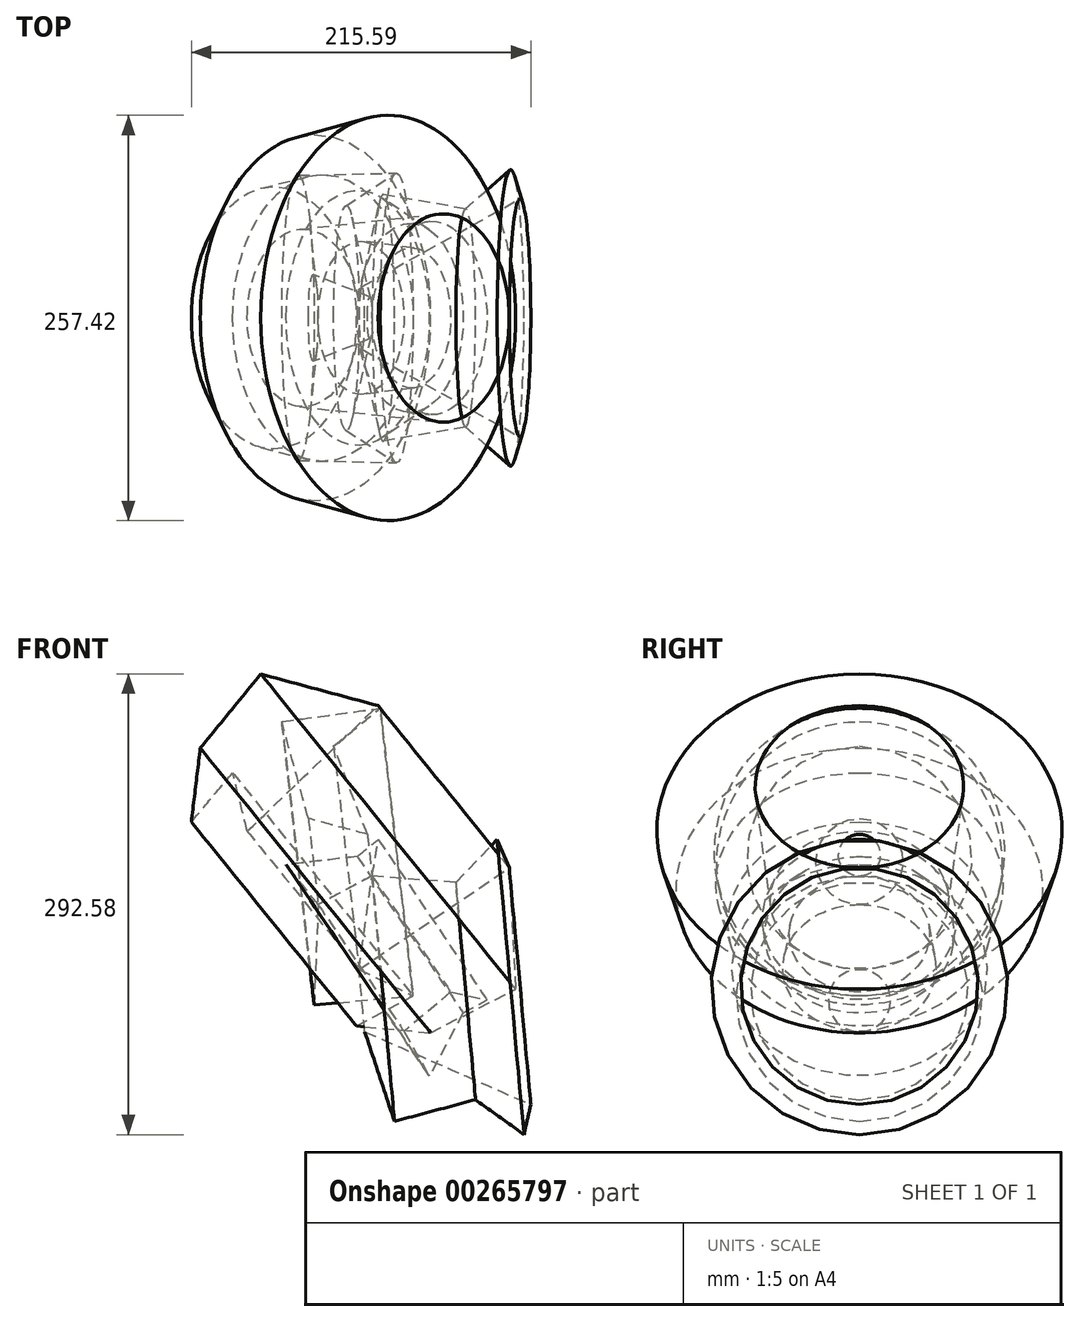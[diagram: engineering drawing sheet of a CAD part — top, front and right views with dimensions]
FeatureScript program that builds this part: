
annotation { "Feature Type Name" : "Feature", "Feature Type Description" : "" }
export const myFeature = defineFeature(function(context is Context, id is Id, definition is map)
    precondition{}
    {
        {
            var Q0;
            Q0=qCreatedBy(makeId("Front.planeOp"),FACE);
            var sketch = newSketch(context, id + "F0", { "sketchPlane" : qUnion([Q0])});
            skLineSegment(sketch, "E0", {"start": v(-31.41, 41.98) * mm, "end": v(-39.7, -17.42) * mm});
            skLineSegment(sketch, "E1", {"start": v(-39.7, -17.42) * mm, "end": v(55.69, 47.12) * mm});
            skLineSegment(sketch, "E2", {"start": v(55.69, 47.12) * mm, "end": v(59.68, -29.99) * mm});
            skLineSegment(sketch, "E3", {"start": v(59.68, -29.99) * mm, "end": v(5.71, -57.69) * mm});
            skLineSegment(sketch, "E4", {"start": v(5.71, -57.69) * mm, "end": v(-41.4, -53.4) * mm});
            skLineSegment(sketch, "E5", {"start": v(-41.4, -53.4) * mm, "end": v(-5.43, -34.27) * mm});
            skLineSegment(sketch, "E6", {"start": v(-5.43, -34.27) * mm, "end": v(-68.25, -39.98) * mm});
            skLineSegment(sketch, "E7", {"start": v(-68.25, -39.98) * mm, "end": v(-65.68, 23.7) * mm});
            skLineSegment(sketch, "E8", {"start": v(-65.68, 23.7) * mm, "end": v(-85.96, 49.12) * mm});
            skLineSegment(sketch, "E9", {"start": v(-85.96, 49.12) * mm, "end": v(-40.84, 54.26) * mm});
            skLineSegment(sketch, "E10", {"start": v(-40.84, 54.26) * mm, "end": v(-27.41, 65.11) * mm});
            skLineSegment(sketch, "E11", {"start": v(-27.41, 65.11) * mm, "end": v(47.98, 65.11) * mm});
            skLineSegment(sketch, "E12", {"start": v(47.98, 65.11) * mm, "end": v(21.7, 37.7) * mm});
            skLineSegment(sketch, "E13", {"start": v(21.7, 37.7) * mm, "end": v(-31.41, 41.98) * mm});
            skLineSegment(sketch, "E14", {"start": v(47.98, 65.11) * mm, "end": v(55.69, 47.12) * mm});
            skLineSegment(sketch, "E15", {"start": v(-41.4, -53.4) * mm, "end": v(-68.25, -39.98) * mm});
            skLineSegment(sketch, "E16", {"start": v(-39.7, -17.42) * mm, "end": v(-5.43, -34.27) * mm});
            skLineSegment(sketch, "E17", {"start": v(-65.68, 23.7) * mm, "end": v(-31.41, 41.98) * mm});
            skLineSegment(sketch, "E18", {"start": v(-31.41, 41.98) * mm, "end": v(-27.41, 65.11) * mm});
            skSolve(sketch);
        }
        {
            var Q0;
            Q0=makeQuery(id+"F0.imprint","IMPRINT",FACE,{"disambiguationData":[TD([[makeQuery(id+"F0.imprint","IMPRINT",EDGE,{"derivedFrom":sQuery(id+"F0.wireOp",EDGE,"E8")}),-1.0]])]});
            var Q1;
            Q1=sQuery(id+"F0.wireOp",EDGE,"E1");
            revolve(context, id + "F1", {"entities" : qUnion([Q0]), "axis" : qUnion([Q1]), "revolveType" : RevolveType.FULL});
        }
        {
            var Q0;
            Q0=makeQuery(id+"F0.imprint","IMPRINT",FACE,{"disambiguationData":[TD([[makeQuery(id+"F0.imprint","IMPRINT",EDGE,{"derivedFrom":sQuery(id+"F0.wireOp",EDGE,"E0")}),-1.0]])]});
            var Q1;
            Q1=sQuery(id+"F0.wireOp",EDGE,"E9");
            revolve(context, id + "F2", {"entities" : qUnion([Q0]), "axis" : qUnion([Q1]), "revolveType" : RevolveType.FULL});
        }
        {
            var Q0;
            Q0=makeQuery(id+"F0.imprint","IMPRINT",FACE,{"disambiguationData":[TD([[makeQuery(id+"F0.imprint","IMPRINT",EDGE,{"derivedFrom":sQuery(id+"F0.wireOp",EDGE,"E1")}),-1.0]])]});
            var Q1;
            Q1=sQuery(id+"F0.wireOp",EDGE,"E10");
            revolve(context, id + "F3", {"entities" : qUnion([Q0]), "axis" : qUnion([Q1]), "revolveType" : RevolveType.FULL});
        }
        {
            var Q0;
            Q0=makeQuery(id+"F0.imprint","IMPRINT",FACE,{"disambiguationData":[TD([[makeQuery(id+"F0.imprint","IMPRINT",EDGE,{"derivedFrom":sQuery(id+"F0.wireOp",EDGE,"E0")}),1.0]])]});
            var Q1;
            Q1=sQuery(id+"F0.wireOp",EDGE,"E6");
            revolve(context, id + "F4", {"entities" : qUnion([Q0]), "axis" : qUnion([Q1]), "revolveType" : RevolveType.FULL});
        }
    });
